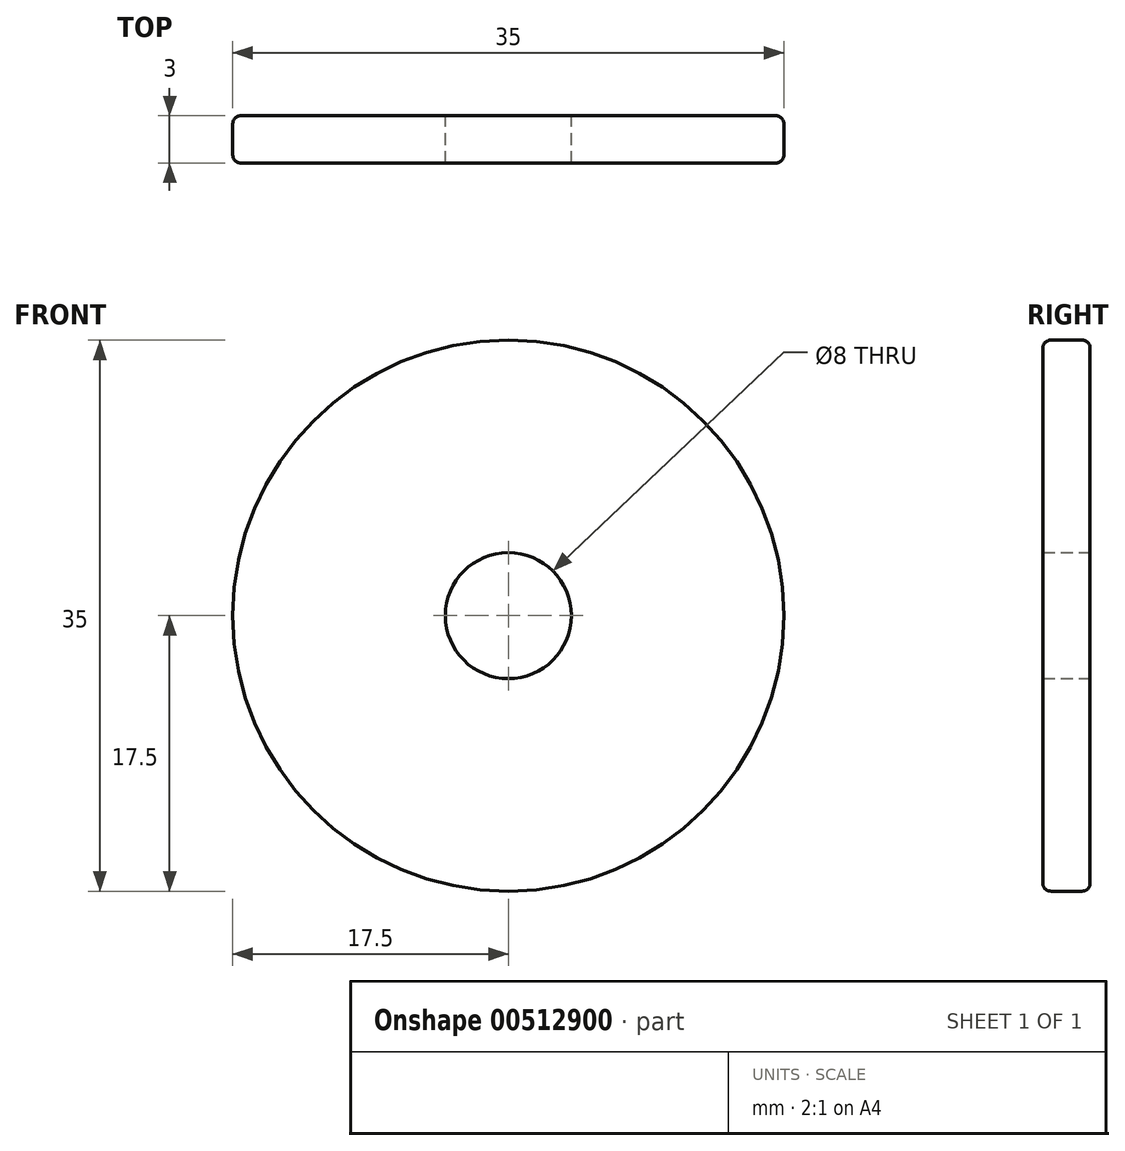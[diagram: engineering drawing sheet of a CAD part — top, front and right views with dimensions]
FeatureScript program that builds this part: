
annotation { "Feature Type Name" : "Feature", "Feature Type Description" : "" }
export const myFeature = defineFeature(function(context is Context, id is Id, definition is map)
    precondition{}
    {
        {
            var Q0;
            Q0=qCreatedBy(makeId("Front.planeOp"),FACE);
            var sketch = newSketch(context, id + "F0", { "sketchPlane" : qUnion([Q0])});
            skCircle(sketch, "E0", {"center": v(0, 0) * mm, "radius": 4 * mm});
            skCircle(sketch, "E1", {"center": v(0, 0) * mm, "radius": 17.5 * mm});
            skSolve(sketch);
        }
        {
            var Q0;
            Q0=makeQuery(id+"F0.imprint","IMPRINT",FACE,{"disambiguationData":[TD([[makeQuery(id+"F0.imprint","IMPRINT",EDGE,{"derivedFrom":sQuery(id+"F0.wireOp",EDGE,"E0")}),-1.0]])]});
            extrude(context, id + "F1", {"entities" : qUnion([Q0]), "depth" : 3 * mm, "offsetDistance" : 25 * mm});
        }
        {
            var Q0;
            Q0=makeQuery(id+"F1.opExtrude","CAP_EDGE",EDGE,{"disambiguationData":[OSD([sQuery(id+"F0.wireOp",EDGE,"E1")])],"isStart":true});
            var Q1;
            Q1=makeQuery(id+"F1.opExtrude","CAP_EDGE",EDGE,{"disambiguationData":[OSD([sQuery(id+"F0.wireOp",EDGE,"E1")])],"isStart":false});
            fillet(context, id + "F2", {"entities" : qUnion([Q0, Q1]), "radius" : .5 * mm, "tangentPropagation" : true, "allowEdgeOverflow" : false});
        }
    });
